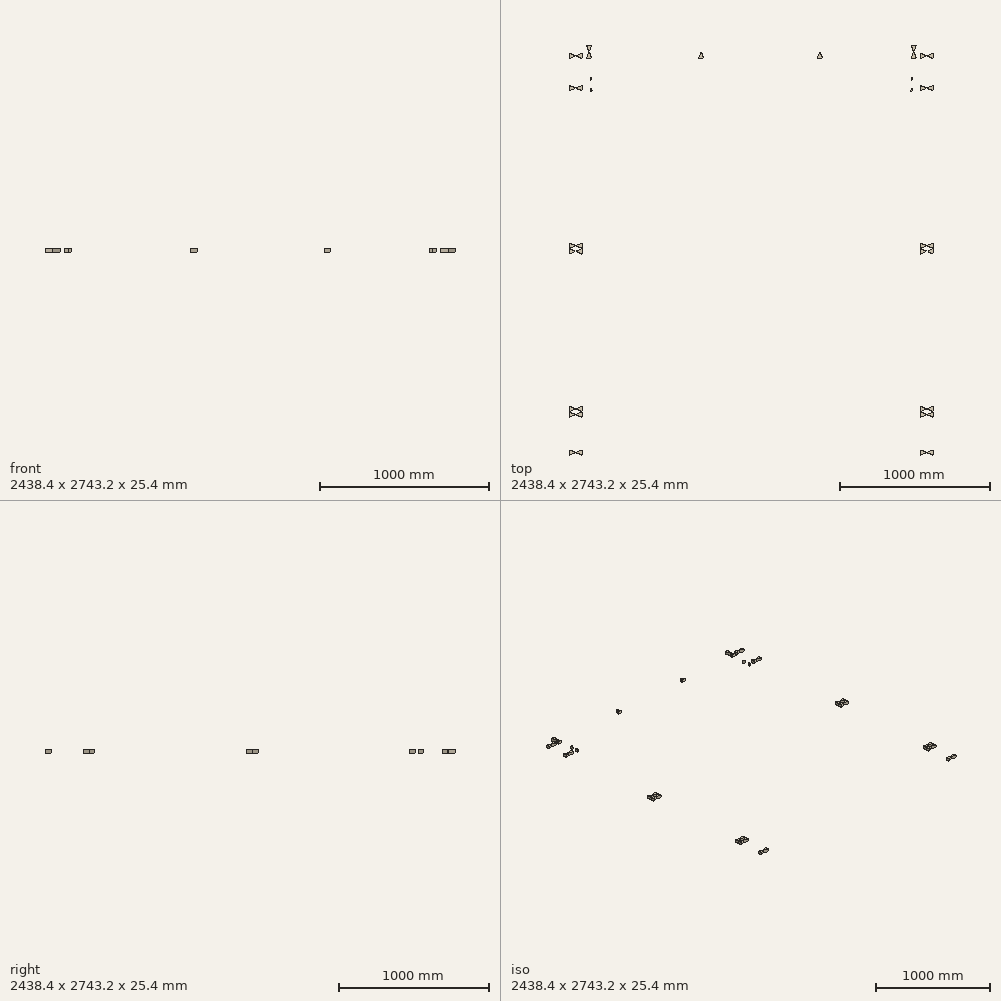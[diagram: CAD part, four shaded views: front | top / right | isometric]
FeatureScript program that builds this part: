
annotation { "Feature Type Name" : "Feature", "Feature Type Description" : "" }
export const myFeature = defineFeature(function(context is Context, id is Id, definition is map)
    precondition{}
    {
        {
            var Q0;
            Q0=qCreatedBy(makeId("Top.planeOp"),FACE);
            var sketch = newSketch(context, id + "F0", { "sketchPlane" : qUnion([Q0])});
            skLineSegment(sketch, "E0.bottom", {"start": v(-1066.8, 0) * mm, "end": v(1066.8, 0) * mm});
            skLineSegment(sketch, "E0.top", {"start": v(-1066.8, -304.8) * mm, "end": v(1066.8, -304.8) * mm, "construction": true});
            skLineSegment(sketch, "E0.left", {"start": v(-1066.8, 0) * mm, "end": v(-1066.8, -304.8) * mm});
            skLineSegment(sketch, "E0.right", {"start": v(1066.8, 0) * mm, "end": v(1066.8, -304.8) * mm});
            skLineSegment(sketch, "E1.bottom", {"start": v(-2001.03, 260.38) * mm, "end": v(-1962.93, 260.38) * mm});
            skLineSegment(sketch, "E1.top", {"start": v(-2001.03, 171.48) * mm, "end": v(-1962.93, 171.48) * mm});
            skLineSegment(sketch, "E1.left", {"start": v(-2001.03, 260.38) * mm, "end": v(-2001.03, 171.48) * mm});
            skLineSegment(sketch, "E1.right", {"start": v(-1962.93, 260.38) * mm, "end": v(-1962.93, 171.48) * mm});
            skLineSegment(sketch, "E2.bottom", {"start": v(-1926.95, 0) * mm, "end": v(-1838.05, 0) * mm});
            skLineSegment(sketch, "E2.top", {"start": v(-1926.95, -38.1) * mm, "end": v(-1838.05, -38.1) * mm});
            skLineSegment(sketch, "E2.left", {"start": v(-1926.95, 0) * mm, "end": v(-1926.95, -38.1) * mm});
            skLineSegment(sketch, "E2.right", {"start": v(-1838.05, 0) * mm, "end": v(-1838.05, -38.1) * mm});
            skLineSegment(sketch, "E3", {"start": v(-2001.03, 260.38) * mm, "end": v(-1962.93, 171.48) * mm});
            skLineSegment(sketch, "E4", {"start": v(-1962.93, 260.38) * mm, "end": v(-2001.03, 171.48) * mm});
            skLineSegment(sketch, "E5", {"start": v(-1926.95, 0) * mm, "end": v(-1838.05, -38.1) * mm});
            skLineSegment(sketch, "E6", {"start": v(-1838.05, 0) * mm, "end": v(-1926.95, -38.1) * mm});
            skLineSegment(sketch, "E7.bottom", {"start": v(-1915.16, -207.44) * mm, "end": v(-1877.06, -207.44) * mm});
            skLineSegment(sketch, "E7.top", {"start": v(-1915.16, -296.34) * mm, "end": v(-1877.06, -296.34) * mm});
            skLineSegment(sketch, "E7.left", {"start": v(-1915.16, -207.44) * mm, "end": v(-1915.16, -296.34) * mm});
            skLineSegment(sketch, "E7.right", {"start": v(-1877.06, -207.44) * mm, "end": v(-1877.06, -296.34) * mm});
            skLineSegment(sketch, "E8", {"start": v(-1915.16, -207.44) * mm, "end": v(-1877.06, -296.34) * mm});
            skLineSegment(sketch, "E9", {"start": v(-1877.06, -207.44) * mm, "end": v(-1915.16, -296.34) * mm});
            skLineSegment(sketch, "E10.bottom", {"start": v(-1104.9, 0) * mm, "end": v(-1066.8, 0) * mm});
            skLineSegment(sketch, "E10.top", {"start": v(-1104.9, -88.9) * mm, "end": v(-1066.8, -88.9) * mm});
            skLineSegment(sketch, "E10.left", {"start": v(-1104.9, 0) * mm, "end": v(-1104.9, -88.9) * mm});
            skLineSegment(sketch, "E10.right", {"start": v(-1066.8, 0) * mm, "end": v(-1066.8, -88.9) * mm});
            skLineSegment(sketch, "E11", {"start": v(-1104.9, 0) * mm, "end": v(-1066.8, -88.9) * mm});
            skLineSegment(sketch, "E12", {"start": v(-1066.8, 0) * mm, "end": v(-1104.9, -88.9) * mm});
            skLineSegment(sketch, "E13.bottom", {"start": v(1066.8, 0) * mm, "end": v(1104.9, 0) * mm});
            skLineSegment(sketch, "E13.top", {"start": v(1066.8, -88.9) * mm, "end": v(1104.9, -88.9) * mm});
            skLineSegment(sketch, "E13.left", {"start": v(1066.8, 0) * mm, "end": v(1066.8, -88.9) * mm});
            skLineSegment(sketch, "E13.right", {"start": v(1104.9, 0) * mm, "end": v(1104.9, -88.9) * mm});
            skLineSegment(sketch, "E14", {"start": v(1066.8, 0) * mm, "end": v(1104.9, -88.9) * mm});
            skLineSegment(sketch, "E15", {"start": v(1104.9, 0) * mm, "end": v(1066.8, -88.9) * mm});
            skLineSegment(sketch, "E16.bottom", {"start": v(-1219.2, -2705.1) * mm, "end": v(-1130.3, -2705.1) * mm});
            skLineSegment(sketch, "E16.top", {"start": v(-1219.2, -2743.2) * mm, "end": v(-1130.3, -2743.2) * mm});
            skLineSegment(sketch, "E16.left", {"start": v(-1219.2, -2705.1) * mm, "end": v(-1219.2, -2743.2) * mm});
            skLineSegment(sketch, "E16.right", {"start": v(-1130.3, -2705.1) * mm, "end": v(-1130.3, -2743.2) * mm});
            skLineSegment(sketch, "E17", {"start": v(-1219.2, -2705.1) * mm, "end": v(-1130.3, -2743.2) * mm});
            skLineSegment(sketch, "E18", {"start": v(-1130.3, -2705.1) * mm, "end": v(-1219.2, -2743.2) * mm});
            skLineSegment(sketch, "E19.bottom", {"start": v(-1219.2, -2451.1) * mm, "end": v(-1130.3, -2451.1) * mm});
            skLineSegment(sketch, "E19.top", {"start": v(-1219.2, -2489.2) * mm, "end": v(-1130.3, -2489.2) * mm});
            skLineSegment(sketch, "E19.left", {"start": v(-1219.2, -2451.1) * mm, "end": v(-1219.2, -2489.2) * mm});
            skLineSegment(sketch, "E19.right", {"start": v(-1130.3, -2451.1) * mm, "end": v(-1130.3, -2489.2) * mm});
            skLineSegment(sketch, "E20", {"start": v(-1219.2, -2451.1) * mm, "end": v(-1130.3, -2489.2) * mm});
            skLineSegment(sketch, "E21", {"start": v(-1130.3, -2451.1) * mm, "end": v(-1219.2, -2489.2) * mm});
            skLineSegment(sketch, "E22.bottom", {"start": v(1130.3, -2451.1) * mm, "end": v(1219.2, -2451.1) * mm});
            skLineSegment(sketch, "E22.top", {"start": v(1130.3, -2489.2) * mm, "end": v(1219.2, -2489.2) * mm});
            skLineSegment(sketch, "E22.left", {"start": v(1130.3, -2451.1) * mm, "end": v(1130.3, -2489.2) * mm});
            skLineSegment(sketch, "E22.right", {"start": v(1219.2, -2451.1) * mm, "end": v(1219.2, -2489.2) * mm});
            skLineSegment(sketch, "E23", {"start": v(1130.3, -2451.1) * mm, "end": v(1219.2, -2489.2) * mm});
            skLineSegment(sketch, "E24", {"start": v(1219.2, -2451.1) * mm, "end": v(1130.3, -2489.2) * mm});
            skLineSegment(sketch, "E25.bottom", {"start": v(-1219.2, -266.7) * mm, "end": v(-1130.3, -266.7) * mm});
            skLineSegment(sketch, "E25.top", {"start": v(-1219.2, -304.8) * mm, "end": v(-1130.3, -304.8) * mm});
            skLineSegment(sketch, "E25.left", {"start": v(-1219.2, -266.7) * mm, "end": v(-1219.2, -304.8) * mm});
            skLineSegment(sketch, "E25.right", {"start": v(-1130.3, -266.7) * mm, "end": v(-1130.3, -304.8) * mm});
            skLineSegment(sketch, "E26", {"start": v(-1219.2, -266.7) * mm, "end": v(-1130.3, -304.8) * mm});
            skLineSegment(sketch, "E27", {"start": v(-1130.3, -266.7) * mm, "end": v(-1219.2, -304.8) * mm});
            skLineSegment(sketch, "E28.bottom", {"start": v(1130.3, -2705.1) * mm, "end": v(1219.2, -2705.1) * mm});
            skLineSegment(sketch, "E28.top", {"start": v(1130.3, -2743.2) * mm, "end": v(1219.2, -2743.2) * mm});
            skLineSegment(sketch, "E28.left", {"start": v(1130.3, -2705.1) * mm, "end": v(1130.3, -2743.2) * mm});
            skLineSegment(sketch, "E28.right", {"start": v(1219.2, -2705.1) * mm, "end": v(1219.2, -2743.2) * mm});
            skLineSegment(sketch, "E29", {"start": v(1130.3, -2705.1) * mm, "end": v(1219.2, -2743.2) * mm});
            skLineSegment(sketch, "E30", {"start": v(1219.2, -2705.1) * mm, "end": v(1130.3, -2743.2) * mm});
            skLineSegment(sketch, "E31.bottom", {"start": v(-1219.2, -1358.9) * mm, "end": v(-1130.3, -1358.9) * mm});
            skLineSegment(sketch, "E31.top", {"start": v(-1219.2, -1397) * mm, "end": v(-1130.3, -1397) * mm});
            skLineSegment(sketch, "E31.left", {"start": v(-1219.2, -1358.9) * mm, "end": v(-1219.2, -1397) * mm});
            skLineSegment(sketch, "E31.right", {"start": v(-1130.3, -1358.9) * mm, "end": v(-1130.3, -1397) * mm});
            skLineSegment(sketch, "E32", {"start": v(-1219.2, -1358.9) * mm, "end": v(-1130.3, -1397) * mm});
            skLineSegment(sketch, "E33", {"start": v(-1130.3, -1358.9) * mm, "end": v(-1219.2, -1397) * mm});
            skLineSegment(sketch, "E34.bottom", {"start": v(1130.3, -1358.9) * mm, "end": v(1219.2, -1358.9) * mm});
            skLineSegment(sketch, "E34.top", {"start": v(1130.3, -1397) * mm, "end": v(1219.2, -1397) * mm});
            skLineSegment(sketch, "E34.left", {"start": v(1130.3, -1358.9) * mm, "end": v(1130.3, -1397) * mm});
            skLineSegment(sketch, "E34.right", {"start": v(1219.2, -1358.9) * mm, "end": v(1219.2, -1397) * mm});
            skLineSegment(sketch, "E35", {"start": v(1130.3, -1358.9) * mm, "end": v(1219.2, -1397) * mm});
            skLineSegment(sketch, "E36", {"start": v(1219.2, -1358.9) * mm, "end": v(1130.3, -1397) * mm});
            skLineSegment(sketch, "E37.bottom", {"start": v(1130.3, -1320.8) * mm, "end": v(1219.2, -1320.8) * mm});
            skLineSegment(sketch, "E37.left", {"start": v(1130.3, -1320.8) * mm, "end": v(1130.3, -1358.9) * mm});
            skLineSegment(sketch, "E37.right", {"start": v(1219.2, -1320.8) * mm, "end": v(1219.2, -1358.9) * mm});
            skLineSegment(sketch, "E38", {"start": v(1130.3, -1320.8) * mm, "end": v(1219.2, -1358.9) * mm});
            skLineSegment(sketch, "E39", {"start": v(1219.2, -1320.8) * mm, "end": v(1130.3, -1358.9) * mm});
            skLineSegment(sketch, "E40.bottom", {"start": v(-1219.2, -1320.8) * mm, "end": v(-1130.3, -1320.8) * mm});
            skLineSegment(sketch, "E40.left", {"start": v(-1219.2, -1320.8) * mm, "end": v(-1219.2, -1358.9) * mm});
            skLineSegment(sketch, "E40.right", {"start": v(-1130.3, -1320.8) * mm, "end": v(-1130.3, -1358.9) * mm});
            skLineSegment(sketch, "E41", {"start": v(-1219.2, -1320.8) * mm, "end": v(-1130.3, -1358.9) * mm});
            skLineSegment(sketch, "E42", {"start": v(-1130.3, -1320.8) * mm, "end": v(-1219.2, -1358.9) * mm});
            skLineSegment(sketch, "E43.bottom", {"start": v(1130.3, -266.7) * mm, "end": v(1219.2, -266.7) * mm});
            skLineSegment(sketch, "E43.top", {"start": v(1130.3, -304.8) * mm, "end": v(1219.2, -304.8) * mm});
            skLineSegment(sketch, "E43.left", {"start": v(1130.3, -266.7) * mm, "end": v(1130.3, -304.8) * mm});
            skLineSegment(sketch, "E43.right", {"start": v(1219.2, -266.7) * mm, "end": v(1219.2, -304.8) * mm});
            skLineSegment(sketch, "E44", {"start": v(1130.3, -266.7) * mm, "end": v(1219.2, -304.8) * mm});
            skLineSegment(sketch, "E45", {"start": v(1219.2, -266.7) * mm, "end": v(1130.3, -304.8) * mm});
            skLineSegment(sketch, "E46.bottom", {"start": v(1130.3, -2413) * mm, "end": v(1219.2, -2413) * mm});
            skLineSegment(sketch, "E46.left", {"start": v(1130.3, -2413) * mm, "end": v(1130.3, -2451.1) * mm});
            skLineSegment(sketch, "E46.right", {"start": v(1219.2, -2413) * mm, "end": v(1219.2, -2451.1) * mm});
            skLineSegment(sketch, "E47", {"start": v(1130.3, -2413) * mm, "end": v(1219.2, -2451.1) * mm});
            skLineSegment(sketch, "E48", {"start": v(1219.2, -2413) * mm, "end": v(1130.3, -2451.1) * mm});
            skLineSegment(sketch, "E49.bottom", {"start": v(-1219.2, -2413) * mm, "end": v(-1130.3, -2413) * mm});
            skLineSegment(sketch, "E49.left", {"start": v(-1219.2, -2413) * mm, "end": v(-1219.2, -2451.1) * mm});
            skLineSegment(sketch, "E49.right", {"start": v(-1130.3, -2413) * mm, "end": v(-1130.3, -2451.1) * mm});
            skLineSegment(sketch, "E50", {"start": v(-1219.2, -2413) * mm, "end": v(-1130.3, -2451.1) * mm});
            skLineSegment(sketch, "E51", {"start": v(-1130.3, -2413) * mm, "end": v(-1219.2, -2451.1) * mm});
            skLineSegment(sketch, "E52.bottom", {"start": v(-2297.54, 110.98) * mm, "end": v(-2195.94, 110.98) * mm});
            skLineSegment(sketch, "E52.top", {"start": v(-2297.54, -905.02) * mm, "end": v(-2195.94, -905.02) * mm});
            skLineSegment(sketch, "E52.left", {"start": v(-2297.54, 110.98) * mm, "end": v(-2297.54, -905.02) * mm});
            skLineSegment(sketch, "E52.right", {"start": v(-2195.94, 110.98) * mm, "end": v(-2195.94, -905.02) * mm});
            skLineSegment(sketch, "E53.bottom", {"start": v(-2586.1, 162.79) * mm, "end": v(-2484.5, 162.79) * mm});
            skLineSegment(sketch, "E53.top", {"start": v(-2586.1, -853.21) * mm, "end": v(-2484.5, -853.21) * mm});
            skLineSegment(sketch, "E53.left", {"start": v(-2586.1, 162.79) * mm, "end": v(-2586.1, -853.21) * mm});
            skLineSegment(sketch, "E53.right", {"start": v(-2484.5, 162.79) * mm, "end": v(-2484.5, -853.21) * mm});
            skLineSegment(sketch, "E54.bottom", {"start": v(-1066.8, 376.5) * mm, "end": v(-1066.8, 478.1) * mm});
            skLineSegment(sketch, "E54.top", {"start": v(-50.8, 376.5) * mm, "end": v(-50.8, 478.1) * mm});
            skLineSegment(sketch, "E54.left", {"start": v(-1066.8, 376.5) * mm, "end": v(-50.8, 376.5) * mm});
            skLineSegment(sketch, "E54.right", {"start": v(-1066.8, 478.1) * mm, "end": v(-50.8, 478.1) * mm});
            skLineSegment(sketch, "E55.bottom", {"start": v(-2346.48, -1244.66) * mm, "end": v(-2244.88, -1244.66) * mm});
            skLineSegment(sketch, "E55.top", {"start": v(-2346.48, -2260.66) * mm, "end": v(-2244.88, -2260.66) * mm});
            skLineSegment(sketch, "E55.left", {"start": v(-2346.48, -1244.66) * mm, "end": v(-2346.48, -2260.66) * mm});
            skLineSegment(sketch, "E55.right", {"start": v(-2244.88, -1244.66) * mm, "end": v(-2244.88, -2260.66) * mm});
            skLineSegment(sketch, "E56.bottom", {"start": v(-1219.2, -1397) * mm, "end": v(-1117.6, -1397) * mm});
            skLineSegment(sketch, "E56.top", {"start": v(-1219.2, -2413) * mm, "end": v(-1117.6, -2413) * mm});
            skLineSegment(sketch, "E56.left", {"start": v(-1219.2, -1397) * mm, "end": v(-1219.2, -2413) * mm});
            skLineSegment(sketch, "E56.right", {"start": v(-1117.6, -1397) * mm, "end": v(-1117.6, -2413) * mm});
            skLineSegment(sketch, "E57.bottom", {"start": v(1117.6, -304.8) * mm, "end": v(1219.2, -304.8) * mm});
            skLineSegment(sketch, "E57.top", {"start": v(1117.6, -1320.8) * mm, "end": v(1219.2, -1320.8) * mm});
            skLineSegment(sketch, "E57.left", {"start": v(1117.6, -304.8) * mm, "end": v(1117.6, -1320.8) * mm});
            skLineSegment(sketch, "E57.right", {"start": v(1219.2, -304.8) * mm, "end": v(1219.2, -1320.8) * mm});
            skLineSegment(sketch, "E58.bottom", {"start": v(1117.6, -1397) * mm, "end": v(1219.2, -1397) * mm});
            skLineSegment(sketch, "E58.top", {"start": v(1117.6, -2413) * mm, "end": v(1219.2, -2413) * mm});
            skLineSegment(sketch, "E58.left", {"start": v(1117.6, -1397) * mm, "end": v(1117.6, -2413) * mm});
            skLineSegment(sketch, "E58.right", {"start": v(1219.2, -1397) * mm, "end": v(1219.2, -2413) * mm});
            skLineSegment(sketch, "E59.bottom", {"start": v(-1219.2, -304.8) * mm, "end": v(-1117.6, -304.8) * mm});
            skLineSegment(sketch, "E59.top", {"start": v(-1219.2, -1320.8) * mm, "end": v(-1117.6, -1320.8) * mm});
            skLineSegment(sketch, "E59.left", {"start": v(-1219.2, -304.8) * mm, "end": v(-1219.2, -1320.8) * mm});
            skLineSegment(sketch, "E59.right", {"start": v(-1117.6, -304.8) * mm, "end": v(-1117.6, -1320.8) * mm});
            skLineSegment(sketch, "E60.bottom", {"start": v(50.8, 376.5) * mm, "end": v(50.8, 478.1) * mm});
            skLineSegment(sketch, "E60.top", {"start": v(1066.8, 376.5) * mm, "end": v(1066.8, 478.1) * mm});
            skLineSegment(sketch, "E60.left", {"start": v(50.8, 376.5) * mm, "end": v(1066.8, 376.5) * mm});
            skLineSegment(sketch, "E60.right", {"start": v(50.8, 478.1) * mm, "end": v(1066.8, 478.1) * mm});
            skLineSegment(sketch, "E61.bottom", {"start": v(-1354.87, -2451.1) * mm, "end": v(-1405.67, -2451.1) * mm});
            skLineSegment(sketch, "E61.top", {"start": v(-1354.87, -152.4) * mm, "end": v(-1405.67, -152.4) * mm});
            skLineSegment(sketch, "E61.left", {"start": v(-1354.87, -2451.1) * mm, "end": v(-1354.87, -152.4) * mm});
            skLineSegment(sketch, "E61.right", {"start": v(-1405.67, -2451.1) * mm, "end": v(-1405.67, -152.4) * mm});
            skLineSegment(sketch, "E62.bottom", {"start": v(2986.33, -1495.33) * mm, "end": v(3087.93, -1495.33) * mm});
            skLineSegment(sketch, "E62.top", {"start": v(2986.33, -2463.75) * mm, "end": v(3087.93, -2463.75) * mm});
            skLineSegment(sketch, "E62.left", {"start": v(2986.33, -1495.33) * mm, "end": v(2986.33, -2463.75) * mm});
            skLineSegment(sketch, "E62.right", {"start": v(3087.93, -1495.33) * mm, "end": v(3087.93, -2463.75) * mm});
            skLineSegment(sketch, "E63", {"start": v(2986.33, -1495.33) * mm, "end": v(3011.73, -1396.95) * mm});
            skLineSegment(sketch, "E64", {"start": v(3011.73, -1396.95) * mm, "end": v(3062.53, -1396.95) * mm});
            skLineSegment(sketch, "E65", {"start": v(3062.53, -1396.95) * mm, "end": v(3087.93, -1495.33) * mm});
            skLineSegment(sketch, "E66.bottom", {"start": v(2863.97, -1645.86) * mm, "end": v(5061.07, -1645.86) * mm});
            skLineSegment(sketch, "E66.top", {"start": v(2863.97, -1747.46) * mm, "end": v(5061.07, -1747.46) * mm});
            skLineSegment(sketch, "E66.left", {"start": v(2863.97, -1645.86) * mm, "end": v(2863.97, -1747.46) * mm});
            skLineSegment(sketch, "E66.right", {"start": v(5061.07, -1645.86) * mm, "end": v(5061.07, -1747.46) * mm});
            skLineSegment(sketch, "E67.bottom", {"start": v(2863.97, -2097.62) * mm, "end": v(5061.07, -2097.62) * mm});
            skLineSegment(sketch, "E67.top", {"start": v(2863.97, -2199.22) * mm, "end": v(5061.07, -2199.22) * mm});
            skLineSegment(sketch, "E67.left", {"start": v(2863.97, -2097.62) * mm, "end": v(2863.97, -2199.22) * mm});
            skLineSegment(sketch, "E67.right", {"start": v(5061.07, -2097.62) * mm, "end": v(5061.07, -2199.22) * mm});
            skLineSegment(sketch, "E68.bottom", {"start": v(2902.07, -12.65) * mm, "end": v(3918.07, -12.65) * mm});
            skLineSegment(sketch, "E68.top", {"start": v(2902.07, -1231.85) * mm, "end": v(3918.07, -1231.85) * mm});
            skLineSegment(sketch, "E68.left", {"start": v(2902.07, -12.65) * mm, "end": v(2902.07, -1231.85) * mm});
            skLineSegment(sketch, "E68.right", {"start": v(3918.07, -12.65) * mm, "end": v(3918.07, -1231.85) * mm});
            skLineSegment(sketch, "E69.bottom", {"start": v(3994.27, -12.65) * mm, "end": v(5010.27, -12.65) * mm});
            skLineSegment(sketch, "E69.top", {"start": v(3994.27, -1231.85) * mm, "end": v(5010.27, -1231.85) * mm});
            skLineSegment(sketch, "E69.left", {"start": v(3994.27, -12.65) * mm, "end": v(3994.27, -1231.85) * mm});
            skLineSegment(sketch, "E69.right", {"start": v(5010.27, -12.65) * mm, "end": v(5010.27, -1231.85) * mm});
            skLineSegment(sketch, "E70.bottom", {"start": v(2902.07, -2451.05) * mm, "end": v(2863.97, -2451.05) * mm});
            skLineSegment(sketch, "E70.top", {"start": v(2902.07, -139.65) * mm, "end": v(2863.97, -139.65) * mm});
            skLineSegment(sketch, "E70.left", {"start": v(2902.07, -2451.05) * mm, "end": v(2902.07, -139.65) * mm});
            skLineSegment(sketch, "E70.right", {"start": v(2863.97, -2451.05) * mm, "end": v(2863.97, -139.65) * mm});
            skLineSegment(sketch, "E71.bottom", {"start": v(2863.97, -2451.05) * mm, "end": v(3956.17, -2451.05) * mm});
            skLineSegment(sketch, "E71.top", {"start": v(2863.97, -2489.15) * mm, "end": v(3956.17, -2489.15) * mm});
            skLineSegment(sketch, "E71.left", {"start": v(2863.97, -2451.05) * mm, "end": v(2863.97, -2489.15) * mm});
            skLineSegment(sketch, "E71.right", {"start": v(3956.17, -2451.05) * mm, "end": v(3956.17, -2489.15) * mm});
            skLineSegment(sketch, "E72.bottom", {"start": v(3918.07, -139.65) * mm, "end": v(3956.17, -139.65) * mm});
            skLineSegment(sketch, "E72.top", {"start": v(3918.07, -2451.05) * mm, "end": v(3956.17, -2451.05) * mm});
            skLineSegment(sketch, "E72.left", {"start": v(3918.07, -139.65) * mm, "end": v(3918.07, -2451.05) * mm});
            skLineSegment(sketch, "E72.right", {"start": v(3956.17, -139.65) * mm, "end": v(3956.17, -2451.05) * mm});
            skLineSegment(sketch, "E73.bottom", {"start": v(3956.17, -12.65) * mm, "end": v(3994.27, -12.65) * mm});
            skLineSegment(sketch, "E73.top", {"start": v(3956.17, -2451.05) * mm, "end": v(3994.27, -2451.05) * mm});
            skLineSegment(sketch, "E73.left", {"start": v(3956.17, -12.65) * mm, "end": v(3956.17, -2451.05) * mm});
            skLineSegment(sketch, "E73.right", {"start": v(3994.27, -12.65) * mm, "end": v(3994.27, -2451.05) * mm});
            skLineSegment(sketch, "E74.bottom", {"start": v(5010.27, -139.65) * mm, "end": v(5048.37, -139.65) * mm});
            skLineSegment(sketch, "E74.top", {"start": v(5010.27, -2451.05) * mm, "end": v(5048.37, -2451.05) * mm});
            skLineSegment(sketch, "E74.left", {"start": v(5010.27, -139.65) * mm, "end": v(5010.27, -2451.05) * mm});
            skLineSegment(sketch, "E74.right", {"start": v(5048.37, -139.65) * mm, "end": v(5048.37, -2451.05) * mm});
            skLineSegment(sketch, "E75.bottom", {"start": v(3956.17, -2489.15) * mm, "end": v(5048.37, -2489.15) * mm});
            skLineSegment(sketch, "E75.top", {"start": v(3956.17, -2451.05) * mm, "end": v(5048.37, -2451.05) * mm});
            skLineSegment(sketch, "E75.left", {"start": v(3956.17, -2489.15) * mm, "end": v(3956.17, -2451.05) * mm});
            skLineSegment(sketch, "E75.right", {"start": v(5048.37, -2489.15) * mm, "end": v(5048.37, -2451.05) * mm});
            skLineSegment(sketch, "E76.bottom", {"start": v(6918.4, -1231.85) * mm, "end": v(9052, -1231.85) * mm});
            skLineSegment(sketch, "E76.top", {"start": v(6918.4, -469.85) * mm, "end": v(9052, -469.85) * mm});
            skLineSegment(sketch, "E76.left", {"start": v(6918.4, -1231.85) * mm, "end": v(6918.4, -469.85) * mm});
            skLineSegment(sketch, "E76.right", {"start": v(9052, -1231.85) * mm, "end": v(9052, -469.85) * mm});
            skLineSegment(sketch, "E77.bottom", {"start": v(6621.52, -12.65) * mm, "end": v(9196.57, -12.65) * mm});
            skLineSegment(sketch, "E77.top", {"start": v(6621.52, -146) * mm, "end": v(9196.57, -146) * mm});
            skLineSegment(sketch, "E77.left", {"start": v(6621.52, -12.65) * mm, "end": v(6621.52, -146) * mm});
            skLineSegment(sketch, "E77.right", {"start": v(9196.57, -12.65) * mm, "end": v(9196.57, -146) * mm});
            skLineSegment(sketch, "E78.bottom", {"start": v(5220.06, -2463.75) * mm, "end": v(5728.06, -2463.75) * mm});
            skLineSegment(sketch, "E78.top", {"start": v(5220.06, -2362.15) * mm, "end": v(5728.06, -2362.15) * mm});
            skLineSegment(sketch, "E78.left", {"start": v(5220.06, -2463.75) * mm, "end": v(5220.06, -2362.15) * mm});
            skLineSegment(sketch, "E78.right", {"start": v(5728.06, -2463.75) * mm, "end": v(5728.06, -2362.15) * mm});
            skLineSegment(sketch, "E79.0.1.0", {"start": v(5728.06, -2273.25) * mm, "end": v(5728.06, -2171.65) * mm});
            skLineSegment(sketch, "E79.0.1.1", {"start": v(5220.06, -2273.25) * mm, "end": v(5220.06, -2171.65) * mm});
            skLineSegment(sketch, "E79.0.1.2", {"start": v(5220.06, -2171.65) * mm, "end": v(5728.06, -2171.65) * mm});
            skLineSegment(sketch, "E79.0.1.3", {"start": v(5220.06, -2273.25) * mm, "end": v(5728.06, -2273.25) * mm});
            skLineSegment(sketch, "E79.0.2.0", {"start": v(5728.06, -2082.75) * mm, "end": v(5728.06, -1981.15) * mm});
            skLineSegment(sketch, "E79.0.2.1", {"start": v(5220.06, -2082.75) * mm, "end": v(5220.06, -1981.15) * mm});
            skLineSegment(sketch, "E79.0.2.2", {"start": v(5220.06, -1981.15) * mm, "end": v(5728.06, -1981.15) * mm});
            skLineSegment(sketch, "E79.0.2.3", {"start": v(5220.06, -2082.75) * mm, "end": v(5728.06, -2082.75) * mm});
            skLineSegment(sketch, "E79.0.3.0", {"start": v(5728.06, -1892.25) * mm, "end": v(5728.06, -1790.65) * mm});
            skLineSegment(sketch, "E79.0.3.1", {"start": v(5220.06, -1892.25) * mm, "end": v(5220.06, -1790.65) * mm});
            skLineSegment(sketch, "E79.0.3.2", {"start": v(5220.06, -1790.65) * mm, "end": v(5728.06, -1790.65) * mm});
            skLineSegment(sketch, "E79.0.3.3", {"start": v(5220.06, -1892.25) * mm, "end": v(5728.06, -1892.25) * mm});
            skLineSegment(sketch, "E79.0.4.0", {"start": v(5728.06, -1701.75) * mm, "end": v(5728.06, -1600.15) * mm});
            skLineSegment(sketch, "E79.0.4.1", {"start": v(5220.06, -1701.75) * mm, "end": v(5220.06, -1600.15) * mm});
            skLineSegment(sketch, "E79.0.4.2", {"start": v(5220.06, -1600.15) * mm, "end": v(5728.06, -1600.15) * mm});
            skLineSegment(sketch, "E79.0.4.3", {"start": v(5220.06, -1701.75) * mm, "end": v(5728.06, -1701.75) * mm});
            skLineSegment(sketch, "E79.0.5.0", {"start": v(5728.06, -1511.25) * mm, "end": v(5728.06, -1409.65) * mm});
            skLineSegment(sketch, "E79.0.5.1", {"start": v(5220.06, -1511.25) * mm, "end": v(5220.06, -1409.65) * mm});
            skLineSegment(sketch, "E79.0.5.2", {"start": v(5220.06, -1409.65) * mm, "end": v(5728.06, -1409.65) * mm});
            skLineSegment(sketch, "E79.0.5.3", {"start": v(5220.06, -1511.25) * mm, "end": v(5728.06, -1511.25) * mm});
            skLineSegment(sketch, "E79.0.6.0", {"start": v(5728.06, -1320.75) * mm, "end": v(5728.06, -1219.15) * mm});
            skLineSegment(sketch, "E79.0.6.1", {"start": v(5220.06, -1320.75) * mm, "end": v(5220.06, -1219.15) * mm});
            skLineSegment(sketch, "E79.0.6.2", {"start": v(5220.06, -1219.15) * mm, "end": v(5728.06, -1219.15) * mm});
            skLineSegment(sketch, "E79.0.6.3", {"start": v(5220.06, -1320.75) * mm, "end": v(5728.06, -1320.75) * mm});
            skLineSegment(sketch, "E79.0.7.0", {"start": v(5728.06, -1130.25) * mm, "end": v(5728.06, -1028.65) * mm});
            skLineSegment(sketch, "E79.0.7.1", {"start": v(5220.06, -1130.25) * mm, "end": v(5220.06, -1028.65) * mm});
            skLineSegment(sketch, "E79.0.7.2", {"start": v(5220.06, -1028.65) * mm, "end": v(5728.06, -1028.65) * mm});
            skLineSegment(sketch, "E79.0.7.3", {"start": v(5220.06, -1130.25) * mm, "end": v(5728.06, -1130.25) * mm});
            skLineSegment(sketch, "E79.0.8.0", {"start": v(5728.06, -939.75) * mm, "end": v(5728.06, -838.15) * mm});
            skLineSegment(sketch, "E79.0.8.1", {"start": v(5220.06, -939.75) * mm, "end": v(5220.06, -838.15) * mm});
            skLineSegment(sketch, "E79.0.8.2", {"start": v(5220.06, -838.15) * mm, "end": v(5728.06, -838.15) * mm});
            skLineSegment(sketch, "E79.0.8.3", {"start": v(5220.06, -939.75) * mm, "end": v(5728.06, -939.75) * mm});
            skLineSegment(sketch, "E79.0.9.0", {"start": v(5728.06, -749.25) * mm, "end": v(5728.06, -647.65) * mm});
            skLineSegment(sketch, "E79.0.9.1", {"start": v(5220.06, -749.25) * mm, "end": v(5220.06, -647.65) * mm});
            skLineSegment(sketch, "E79.0.9.2", {"start": v(5220.06, -647.65) * mm, "end": v(5728.06, -647.65) * mm});
            skLineSegment(sketch, "E79.0.9.3", {"start": v(5220.06, -749.25) * mm, "end": v(5728.06, -749.25) * mm});
            skLineSegment(sketch, "E79.0.10.0", {"start": v(5728.06, -558.75) * mm, "end": v(5728.06, -457.15) * mm});
            skLineSegment(sketch, "E79.0.10.1", {"start": v(5220.06, -558.75) * mm, "end": v(5220.06, -457.15) * mm});
            skLineSegment(sketch, "E79.0.10.2", {"start": v(5220.06, -457.15) * mm, "end": v(5728.06, -457.15) * mm});
            skLineSegment(sketch, "E79.0.10.3", {"start": v(5220.06, -558.75) * mm, "end": v(5728.06, -558.75) * mm});
            skLineSegment(sketch, "E79.0.11.0", {"start": v(5728.06, -368.25) * mm, "end": v(5728.06, -266.65) * mm});
            skLineSegment(sketch, "E79.0.11.1", {"start": v(5220.06, -368.25) * mm, "end": v(5220.06, -266.65) * mm});
            skLineSegment(sketch, "E79.0.11.2", {"start": v(5220.06, -266.65) * mm, "end": v(5728.06, -266.65) * mm});
            skLineSegment(sketch, "E79.0.11.3", {"start": v(5220.06, -368.25) * mm, "end": v(5728.06, -368.25) * mm});
            skLineSegment(sketch, "E79.direction1", {"start": v(5220.06, -2463.75) * mm, "end": v(5223, -2463.75) * mm, "construction": true});
            skLineSegment(sketch, "E79.direction2", {"start": v(5220.06, -2463.75) * mm, "end": v(5220.06, -2273.25) * mm, "construction": true});
            skLineSegment(sketch, "E80.bottom", {"start": v(-1104.9, -215.9) * mm, "end": v(-1066.8, -215.9) * mm});
            skLineSegment(sketch, "E80.top", {"start": v(-1104.9, -304.8) * mm, "end": v(-1066.8, -304.8) * mm});
            skLineSegment(sketch, "E80.left", {"start": v(-1104.9, -215.9) * mm, "end": v(-1104.9, -304.8) * mm});
            skLineSegment(sketch, "E80.right", {"start": v(-1066.8, -215.9) * mm, "end": v(-1066.8, -304.8) * mm});
            skLineSegment(sketch, "E81", {"start": v(-1104.9, -215.9) * mm, "end": v(-1066.8, -304.8) * mm});
            skLineSegment(sketch, "E82", {"start": v(-1066.8, -215.9) * mm, "end": v(-1104.9, -304.8) * mm});
            skLineSegment(sketch, "E83.bottom", {"start": v(1066.8, -215.9) * mm, "end": v(1104.9, -215.9) * mm});
            skLineSegment(sketch, "E83.top", {"start": v(1066.8, -304.8) * mm, "end": v(1104.9, -304.8) * mm});
            skLineSegment(sketch, "E83.left", {"start": v(1066.8, -215.9) * mm, "end": v(1066.8, -304.8) * mm});
            skLineSegment(sketch, "E83.right", {"start": v(1104.9, -215.9) * mm, "end": v(1104.9, -304.8) * mm});
            skLineSegment(sketch, "E84", {"start": v(1066.8, -215.9) * mm, "end": v(1104.9, -304.8) * mm});
            skLineSegment(sketch, "E85", {"start": v(1104.9, -215.9) * mm, "end": v(1066.8, -304.8) * mm});
            skLineSegment(sketch, "E86.bottom", {"start": v(-355.42, 0) * mm, "end": v(-317.32, 0) * mm});
            skLineSegment(sketch, "E86.top", {"start": v(-355.42, -88.9) * mm, "end": v(-317.32, -88.9) * mm});
            skLineSegment(sketch, "E86.left", {"start": v(-355.42, 0) * mm, "end": v(-355.42, -88.9) * mm});
            skLineSegment(sketch, "E86.right", {"start": v(-317.32, 0) * mm, "end": v(-317.32, -88.9) * mm});
            skLineSegment(sketch, "E87", {"start": v(-355.42, 0) * mm, "end": v(-317.32, -88.9) * mm});
            skLineSegment(sketch, "E88", {"start": v(-317.32, 0) * mm, "end": v(-355.42, -88.9) * mm});
            skLineSegment(sketch, "E89.bottom", {"start": v(439.21, 0) * mm, "end": v(477.31, 0) * mm});
            skLineSegment(sketch, "E89.top", {"start": v(439.21, -88.9) * mm, "end": v(477.31, -88.9) * mm});
            skLineSegment(sketch, "E89.left", {"start": v(439.21, 0) * mm, "end": v(439.21, -88.9) * mm});
            skLineSegment(sketch, "E89.right", {"start": v(477.31, 0) * mm, "end": v(477.31, -88.9) * mm});
            skLineSegment(sketch, "E90", {"start": v(439.21, 0) * mm, "end": v(477.31, -88.9) * mm});
            skLineSegment(sketch, "E91", {"start": v(477.31, 0) * mm, "end": v(439.21, -88.9) * mm});
            skLineSegment(sketch, "E92.bottom", {"start": v(-1219.2, -50.8) * mm, "end": v(-1130.3, -50.8) * mm});
            skLineSegment(sketch, "E92.top", {"start": v(-1219.2, -88.9) * mm, "end": v(-1130.3, -88.9) * mm});
            skLineSegment(sketch, "E92.left", {"start": v(-1219.2, -50.8) * mm, "end": v(-1219.2, -88.9) * mm});
            skLineSegment(sketch, "E92.right", {"start": v(-1130.3, -50.8) * mm, "end": v(-1130.3, -88.9) * mm});
            skLineSegment(sketch, "E93", {"start": v(-1219.2, -50.8) * mm, "end": v(-1130.3, -88.9) * mm});
            skLineSegment(sketch, "E94", {"start": v(-1130.3, -50.8) * mm, "end": v(-1219.2, -88.9) * mm});
            skLineSegment(sketch, "E95.bottom", {"start": v(1130.3, -50.8) * mm, "end": v(1219.2, -50.8) * mm});
            skLineSegment(sketch, "E95.top", {"start": v(1130.3, -88.9) * mm, "end": v(1219.2, -88.9) * mm});
            skLineSegment(sketch, "E95.left", {"start": v(1130.3, -50.8) * mm, "end": v(1130.3, -88.9) * mm});
            skLineSegment(sketch, "E95.right", {"start": v(1219.2, -50.8) * mm, "end": v(1219.2, -88.9) * mm});
            skLineSegment(sketch, "E96", {"start": v(1130.3, -50.8) * mm, "end": v(1219.2, -88.9) * mm});
            skLineSegment(sketch, "E97", {"start": v(1219.2, -50.8) * mm, "end": v(1130.3, -88.9) * mm});
            skLineSegment(sketch, "E98.top", {"start": v(-1130.3, -152.4) * mm, "end": v(-1079.5, -152.4) * mm});
            skLineSegment(sketch, "E98.left", {"start": v(-1130.3, -612.8) * mm, "end": v(-1130.3, -152.4) * mm});
            skLineSegment(sketch, "E98.right", {"start": v(-1079.5, -612.8) * mm, "end": v(-1079.5, -152.4) * mm});
            skLineSegment(sketch, "E99.top", {"start": v(1130.3, -621.08) * mm, "end": v(1079.5, -621.08) * mm});
            skLineSegment(sketch, "E99.left", {"start": v(1130.3, -152.4) * mm, "end": v(1130.3, -621.08) * mm});
            skLineSegment(sketch, "E99.right", {"start": v(1079.5, -152.4) * mm, "end": v(1079.5, -621.08) * mm});
            skLineSegment(sketch, "E100", {"start": v(-1130.3, -612.8) * mm, "end": v(-1079.5, -612.8) * mm});
            skLineSegment(sketch, "E101", {"start": v(1079.5, -152.4) * mm, "end": v(1130.3, -152.4) * mm});
            skSolve(sketch);
        }
        {
            var Q0;
            {var subQ0=sQuery(id+"F0.wireOp",EDGE,"E16.left");Q0=makeQuery(id+"F0.imprint","IMPRINT",FACE,{"disambiguationData":[TD([[makeQuery(id+"F0.imprint","IMPRINT",EDGE,{"derivedFrom":subQ0}),1.0]])]});}
            var Q1;
            {var subQ0=sQuery(id+"F0.wireOp",EDGE,"E16.right");Q1=makeQuery(id+"F0.imprint","IMPRINT",FACE,{"disambiguationData":[TD([[makeQuery(id+"F0.imprint","IMPRINT",EDGE,{"derivedFrom":subQ0}),-1.0]])]});}
            var Q2;
            {var subQ0=sQuery(id+"F0.wireOp",EDGE,"E19.left");Q2=makeQuery(id+"F0.imprint","IMPRINT",FACE,{"disambiguationData":[TD([[makeQuery(id+"F0.imprint","IMPRINT",EDGE,{"derivedFrom":subQ0}),1.0]])]});}
            var Q3;
            {var subQ0=sQuery(id+"F0.wireOp",EDGE,"E19.right");Q3=makeQuery(id+"F0.imprint","IMPRINT",FACE,{"disambiguationData":[TD([[makeQuery(id+"F0.imprint","IMPRINT",EDGE,{"derivedFrom":subQ0}),-1.0]])]});}
            var Q4;
            {var subQ0=sQuery(id+"F0.wireOp",EDGE,"E49.right");Q4=makeQuery(id+"F0.imprint","IMPRINT",FACE,{"disambiguationData":[TD([[makeQuery(id+"F0.imprint","IMPRINT",EDGE,{"derivedFrom":subQ0}),-1.0]])]});}
            var Q5;
            {var subQ0=sQuery(id+"F0.wireOp",EDGE,"E49.left");Q5=makeQuery(id+"F0.imprint","IMPRINT",FACE,{"disambiguationData":[TD([[makeQuery(id+"F0.imprint","IMPRINT",EDGE,{"derivedFrom":subQ0}),1.0]])]});}
            var Q6;
            {var subQ0=sQuery(id+"F0.wireOp",EDGE,"E28.right");Q6=makeQuery(id+"F0.imprint","IMPRINT",FACE,{"disambiguationData":[TD([[makeQuery(id+"F0.imprint","IMPRINT",EDGE,{"derivedFrom":subQ0}),-1.0]])]});}
            var Q7;
            {var subQ0=sQuery(id+"F0.wireOp",EDGE,"E28.left");Q7=makeQuery(id+"F0.imprint","IMPRINT",FACE,{"disambiguationData":[TD([[makeQuery(id+"F0.imprint","IMPRINT",EDGE,{"derivedFrom":subQ0}),1.0]])]});}
            var Q8;
            {var subQ0=sQuery(id+"F0.wireOp",EDGE,"E22.left");Q8=makeQuery(id+"F0.imprint","IMPRINT",FACE,{"disambiguationData":[TD([[makeQuery(id+"F0.imprint","IMPRINT",EDGE,{"derivedFrom":subQ0}),1.0]])]});}
            var Q9;
            {var subQ0=sQuery(id+"F0.wireOp",EDGE,"E22.right");Q9=makeQuery(id+"F0.imprint","IMPRINT",FACE,{"disambiguationData":[TD([[makeQuery(id+"F0.imprint","IMPRINT",EDGE,{"derivedFrom":subQ0}),-1.0]])]});}
            var Q10;
            {var subQ0=sQuery(id+"F0.wireOp",EDGE,"E46.right");Q10=makeQuery(id+"F0.imprint","IMPRINT",FACE,{"disambiguationData":[TD([[makeQuery(id+"F0.imprint","IMPRINT",EDGE,{"derivedFrom":subQ0}),-1.0]])]});}
            var Q11;
            {var subQ0=sQuery(id+"F0.wireOp",EDGE,"E46.left");Q11=makeQuery(id+"F0.imprint","IMPRINT",FACE,{"disambiguationData":[TD([[makeQuery(id+"F0.imprint","IMPRINT",EDGE,{"derivedFrom":subQ0}),1.0]])]});}
            var Q12;
            {var subQ0=sQuery(id+"F0.wireOp",EDGE,"E40.left");Q12=makeQuery(id+"F0.imprint","IMPRINT",FACE,{"disambiguationData":[TD([[makeQuery(id+"F0.imprint","IMPRINT",EDGE,{"derivedFrom":subQ0}),1.0]])]});}
            var Q13;
            {var subQ0=sQuery(id+"F0.wireOp",EDGE,"E31.left");Q13=makeQuery(id+"F0.imprint","IMPRINT",FACE,{"disambiguationData":[TD([[makeQuery(id+"F0.imprint","IMPRINT",EDGE,{"derivedFrom":subQ0}),1.0]])]});}
            var Q14;
            {var subQ0=sQuery(id+"F0.wireOp",EDGE,"E31.right");Q14=makeQuery(id+"F0.imprint","IMPRINT",FACE,{"disambiguationData":[TD([[makeQuery(id+"F0.imprint","IMPRINT",EDGE,{"derivedFrom":subQ0}),-1.0]])]});}
            var Q15;
            {var subQ0=sQuery(id+"F0.wireOp",EDGE,"E40.right");Q15=makeQuery(id+"F0.imprint","IMPRINT",FACE,{"disambiguationData":[TD([[makeQuery(id+"F0.imprint","IMPRINT",EDGE,{"derivedFrom":subQ0}),-1.0]])]});}
            var Q16;
            {var subQ0=sQuery(id+"F0.wireOp",EDGE,"E37.left");Q16=makeQuery(id+"F0.imprint","IMPRINT",FACE,{"disambiguationData":[TD([[makeQuery(id+"F0.imprint","IMPRINT",EDGE,{"derivedFrom":subQ0}),1.0]])]});}
            var Q17;
            {var subQ0=sQuery(id+"F0.wireOp",EDGE,"E37.right");Q17=makeQuery(id+"F0.imprint","IMPRINT",FACE,{"disambiguationData":[TD([[makeQuery(id+"F0.imprint","IMPRINT",EDGE,{"derivedFrom":subQ0}),-1.0]])]});}
            var Q18;
            {var subQ0=sQuery(id+"F0.wireOp",EDGE,"E34.right");Q18=makeQuery(id+"F0.imprint","IMPRINT",FACE,{"disambiguationData":[TD([[makeQuery(id+"F0.imprint","IMPRINT",EDGE,{"derivedFrom":subQ0}),-1.0]])]});}
            var Q19;
            {var subQ0=sQuery(id+"F0.wireOp",EDGE,"E34.left");Q19=makeQuery(id+"F0.imprint","IMPRINT",FACE,{"disambiguationData":[TD([[makeQuery(id+"F0.imprint","IMPRINT",EDGE,{"derivedFrom":subQ0}),1.0]])]});}
            var Q20;
            {var subQ0=sQuery(id+"F0.wireOp",EDGE,"E13.bottom");Q20=makeQuery(id+"F0.imprint","IMPRINT",FACE,{"disambiguationData":[TD([[makeQuery(id+"F0.imprint","IMPRINT",EDGE,{"derivedFrom":subQ0}),-1.0]])]});}
            var Q21;
            {var subQ0=sQuery(id+"F0.wireOp",EDGE,"E13.top");Q21=makeQuery(id+"F0.imprint","IMPRINT",FACE,{"disambiguationData":[TD([[makeQuery(id+"F0.imprint","IMPRINT",EDGE,{"derivedFrom":subQ0}),1.0]])]});}
            var Q22;
            {var subQ0=sQuery(id+"F0.wireOp",EDGE,"cd718e3a-a49f-493c-a5a9-b7b95544caf7.bottom");Q22=makeQuery(id+"F0.imprint","IMPRINT",FACE,{"disambiguationData":[TD([[makeQuery(id+"F0.imprint","IMPRINT",EDGE,{"derivedFrom":subQ0}),-1.0]])]});}
            var Q23;
            {var subQ0=sQuery(id+"F0.wireOp",EDGE,"cd718e3a-a49f-493c-a5a9-b7b95544caf7.top");Q23=makeQuery(id+"F0.imprint","IMPRINT",FACE,{"disambiguationData":[TD([[makeQuery(id+"F0.imprint","IMPRINT",EDGE,{"derivedFrom":subQ0}),1.0]])]});}
            var Q24;
            {var subQ0=sQuery(id+"F0.wireOp",EDGE,"E43.right");Q24=makeQuery(id+"F0.imprint","IMPRINT",FACE,{"disambiguationData":[TD([[makeQuery(id+"F0.imprint","IMPRINT",EDGE,{"derivedFrom":subQ0}),-1.0]])]});}
            var Q25;
            {var subQ0=sQuery(id+"F0.wireOp",EDGE,"E43.left");Q25=makeQuery(id+"F0.imprint","IMPRINT",FACE,{"disambiguationData":[TD([[makeQuery(id+"F0.imprint","IMPRINT",EDGE,{"derivedFrom":subQ0}),1.0]])]});}
            var Q26;
            {var subQ0=sQuery(id+"F0.wireOp",EDGE,"e7a048e9-28d3-4a94-a536-3ff933cb976e.bottom");Q26=makeQuery(id+"F0.imprint","IMPRINT",FACE,{"disambiguationData":[TD([[makeQuery(id+"F0.imprint","IMPRINT",EDGE,{"derivedFrom":subQ0}),-1.0]])]});}
            var Q27;
            {var subQ0=sQuery(id+"F0.wireOp",EDGE,"e7a048e9-28d3-4a94-a536-3ff933cb976e.top");Q27=makeQuery(id+"F0.imprint","IMPRINT",FACE,{"disambiguationData":[TD([[makeQuery(id+"F0.imprint","IMPRINT",EDGE,{"derivedFrom":subQ0}),1.0]])]});}
            var Q28;
            {var subQ0=sQuery(id+"F0.wireOp",EDGE,"E10.bottom");Q28=makeQuery(id+"F0.imprint","IMPRINT",FACE,{"disambiguationData":[TD([[makeQuery(id+"F0.imprint","IMPRINT",EDGE,{"derivedFrom":subQ0}),-1.0]])]});}
            var Q29;
            {var subQ0=sQuery(id+"F0.wireOp",EDGE,"E10.top");Q29=makeQuery(id+"F0.imprint","IMPRINT",FACE,{"disambiguationData":[TD([[makeQuery(id+"F0.imprint","IMPRINT",EDGE,{"derivedFrom":subQ0}),1.0]])]});}
            var Q30;
            {var subQ0=sQuery(id+"F0.wireOp",EDGE,"E25.left");Q30=makeQuery(id+"F0.imprint","IMPRINT",FACE,{"disambiguationData":[TD([[makeQuery(id+"F0.imprint","IMPRINT",EDGE,{"derivedFrom":subQ0}),1.0]])]});}
            var Q31;
            {var subQ0=sQuery(id+"F0.wireOp",EDGE,"E25.right");Q31=makeQuery(id+"F0.imprint","IMPRINT",FACE,{"disambiguationData":[TD([[makeQuery(id+"F0.imprint","IMPRINT",EDGE,{"derivedFrom":subQ0}),-1.0]])]});}
            var Q32;
            {var subQ0=sQuery(id+"F0.wireOp",EDGE,"E80.bottom");Q32=makeQuery(id+"F0.imprint","IMPRINT",FACE,{"disambiguationData":[TD([[makeQuery(id+"F0.imprint","IMPRINT",EDGE,{"derivedFrom":subQ0}),-1.0]])]});}
            var Q33;
            {var subQ0=sQuery(id+"F0.wireOp",EDGE,"E80.top");Q33=makeQuery(id+"F0.imprint","IMPRINT",FACE,{"disambiguationData":[TD([[makeQuery(id+"F0.imprint","IMPRINT",EDGE,{"derivedFrom":subQ0}),1.0]])]});}
            var Q34;
            {var subQ0=sQuery(id+"F0.wireOp",EDGE,"E83.bottom");Q34=makeQuery(id+"F0.imprint","IMPRINT",FACE,{"disambiguationData":[TD([[makeQuery(id+"F0.imprint","IMPRINT",EDGE,{"derivedFrom":subQ0}),-1.0]])]});}
            var Q35;
            {var subQ0=sQuery(id+"F0.wireOp",EDGE,"E83.top");Q35=makeQuery(id+"F0.imprint","IMPRINT",FACE,{"disambiguationData":[TD([[makeQuery(id+"F0.imprint","IMPRINT",EDGE,{"derivedFrom":subQ0}),1.0]])]});}
            var Q36;
            {var subQ0=sQuery(id+"F0.wireOp",EDGE,"E89.bottom");Q36=makeQuery(id+"F0.imprint","IMPRINT",FACE,{"disambiguationData":[TD([[makeQuery(id+"F0.imprint","IMPRINT",EDGE,{"derivedFrom":subQ0}),-1.0]])]});}
            var Q37;
            {var subQ0=sQuery(id+"F0.wireOp",EDGE,"E89.top");Q37=makeQuery(id+"F0.imprint","IMPRINT",FACE,{"disambiguationData":[TD([[makeQuery(id+"F0.imprint","IMPRINT",EDGE,{"derivedFrom":subQ0}),1.0]])]});}
            var Q38;
            {var subQ0=sQuery(id+"F0.wireOp",EDGE,"E86.bottom");Q38=makeQuery(id+"F0.imprint","IMPRINT",FACE,{"disambiguationData":[TD([[makeQuery(id+"F0.imprint","IMPRINT",EDGE,{"derivedFrom":subQ0}),-1.0]])]});}
            var Q39;
            {var subQ0=sQuery(id+"F0.wireOp",EDGE,"E86.top");Q39=makeQuery(id+"F0.imprint","IMPRINT",FACE,{"disambiguationData":[TD([[makeQuery(id+"F0.imprint","IMPRINT",EDGE,{"derivedFrom":subQ0}),1.0]])]});}
            var Q40;
            {var subQ0=sQuery(id+"F0.wireOp",EDGE,"E95.left");Q40=makeQuery(id+"F0.imprint","IMPRINT",FACE,{"disambiguationData":[TD([[makeQuery(id+"F0.imprint","IMPRINT",EDGE,{"derivedFrom":subQ0}),1.0]])]});}
            var Q41;
            {var subQ0=sQuery(id+"F0.wireOp",EDGE,"E95.right");Q41=makeQuery(id+"F0.imprint","IMPRINT",FACE,{"disambiguationData":[TD([[makeQuery(id+"F0.imprint","IMPRINT",EDGE,{"derivedFrom":subQ0}),-1.0]])]});}
            var Q42;
            {var subQ0=sQuery(id+"F0.wireOp",EDGE,"E92.left");Q42=makeQuery(id+"F0.imprint","IMPRINT",FACE,{"disambiguationData":[TD([[makeQuery(id+"F0.imprint","IMPRINT",EDGE,{"derivedFrom":subQ0}),1.0]])]});}
            var Q43;
            {var subQ0=sQuery(id+"F0.wireOp",EDGE,"E92.right");Q43=makeQuery(id+"F0.imprint","IMPRINT",FACE,{"disambiguationData":[TD([[makeQuery(id+"F0.imprint","IMPRINT",EDGE,{"derivedFrom":subQ0}),-1.0]])]});}
            extrude(context, id + "F1", {"entities" : qUnion([Q0, Q1, Q2, Q3, Q4, Q5, Q6, Q7, Q8, Q9, Q10, Q11, Q12, Q13, Q14, Q15, Q16, Q17, Q18, Q19, Q20, Q21, Q22, Q23, Q24, Q25, Q26, Q27, Q28, Q29, Q30, Q31, Q32, Q33, Q34, Q35, Q36, Q37, Q38, Q39, Q40, Q41, Q42, Q43]), "depth" : 25.4 * mm, "offsetDistance" : 25.4 * mm});
        }
    });
